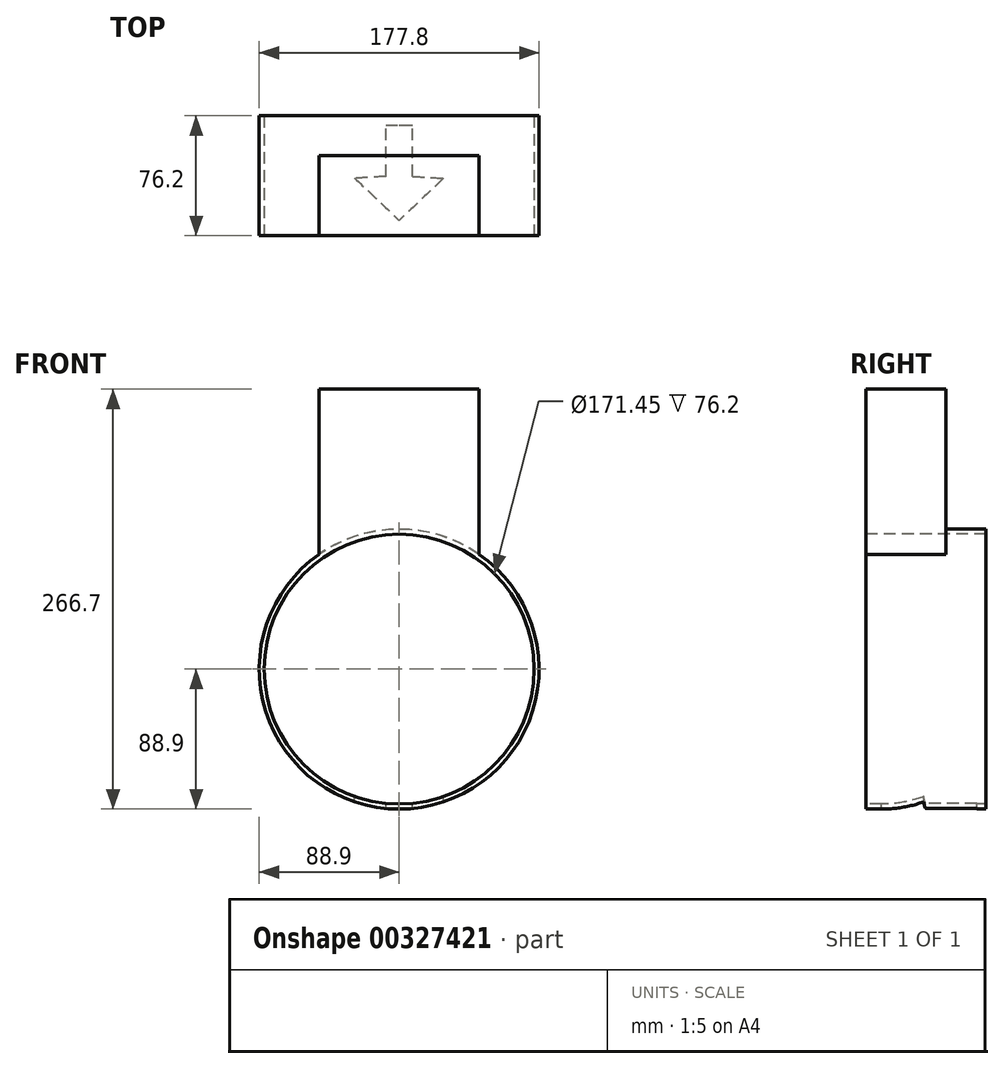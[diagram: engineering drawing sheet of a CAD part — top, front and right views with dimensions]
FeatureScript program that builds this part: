
annotation { "Feature Type Name" : "Feature", "Feature Type Description" : "" }
export const myFeature = defineFeature(function(context is Context, id is Id, definition is map)
    precondition{}
    {
        {
            var Q0;
            Q0=qCreatedBy(makeId("Front.planeOp"),FACE);
            var sketch = newSketch(context, id + "F0", { "sketchPlane" : qUnion([Q0])});
            skCircle(sketch, "E0", {"center": v(0, 0) * mm, "radius": 88.9 * mm});
            skSolve(sketch);
        }
        {
            var Q0;
            Q0 = qSketchRegion(id + "F0", true);
            extrude(context, id + "F1", {"entities" : qUnion([Q0]), "depth" : 76.2 * mm});
        }
        {
            var Q0;
            Q0=qCreatedBy(makeId("Top.planeOp"),FACE);
            var sketch = newSketch(context, id + "F2", { "sketchPlane" : qUnion([Q0])});
            skLineSegment(sketch, "E1.bottom", {"start": v(-50.8, -25.4) * mm, "end": v(50.8, -25.4) * mm});
            skLineSegment(sketch, "E1.top", {"start": v(-50.8, -76.2) * mm, "end": v(50.8, -76.2) * mm});
            skLineSegment(sketch, "E1.left", {"start": v(-50.8, -25.4) * mm, "end": v(-50.8, -76.2) * mm});
            skLineSegment(sketch, "E1.right", {"start": v(50.8, -25.4) * mm, "end": v(50.8, -76.2) * mm});
            skPoint(sketch, "E2", {"position": v(0, -25.4) * mm});
            skSolve(sketch);
        }
        {
            var Q0;
            Q0 = qSketchRegion(id + "F2", true);
            extrude(context, id + "F3", {"entities" : qUnion([Q0]), "operationType" : NewBodyOperationType.ADD, "depth" : 177.8 * mm});
        }
        {
            var Q0;
            Q0=qCreatedBy(makeId("Top.planeOp"),FACE);
            var sketch = newSketch(context, id + "F4", { "sketchPlane" : qUnion([Q0])});
            skLineSegment(sketch, "E3", {"start": v(0, -5.84) * mm, "end": v(-8.47, -5.84) * mm});
            skLineSegment(sketch, "E4", {"start": v(-8.47, -38.51) * mm, "end": v(-8.47, -5.84) * mm});
            skLineSegment(sketch, "E5", {"start": v(-8.47, -38.51) * mm, "end": v(-28.22, -39.67) * mm});
            skLineSegment(sketch, "E6", {"start": v(-28.22, -39.67) * mm, "end": v(0, -66.44) * mm});
            skLineSegment(sketch, "E7.MirrorCS", {"start": v(28.22, -39.67) * mm, "end": v(0, -66.44) * mm});
            skLineSegment(sketch, "E8.MirrorCS", {"start": v(8.47, -38.51) * mm, "end": v(28.22, -39.67) * mm});
            skLineSegment(sketch, "E9.MirrorCS", {"start": v(8.47, -38.51) * mm, "end": v(8.47, -5.84) * mm});
            skLineSegment(sketch, "E10.MirrorCS", {"start": v(0, -5.84) * mm, "end": v(8.47, -5.84) * mm});
            skSolve(sketch);
        }
        {
            var Q0;
            Q0 = qSketchRegion(id + "F4", true);
            extrude(context, id + "F5", {"entities" : qUnion([Q0]), "operationType" : NewBodyOperationType.REMOVE, "oppositeDirection" : true, "depth" : 304.8 * mm});
        }
        {
            var Q0;
            Q0=makeQuery(id+"F1.opExtrude","CAP_FACE",FACE,{"disambiguationData":[OSD([sQuery(id+"F0.wireOp",EDGE,"E0")])],"isStart":false});
            var sketch = newSketch(context, id + "F6", { "sketchPlane" : qUnion([Q0])});
            skCircle(sketch, "E11", {"center": v(0, 0) * mm, "radius": 85.73 * mm});
            skSolve(sketch);
        }
        {
            var Q0;
            Q0 = qSketchRegion(id + "F6", true);
            extrude(context, id + "F7", {"entities" : qUnion([Q0]), "operationType" : NewBodyOperationType.REMOVE, "endBound" : BoundingType.THROUGH_ALL, "oppositeDirection" : true, "depth" : 25.4 * mm});
        }
    });
